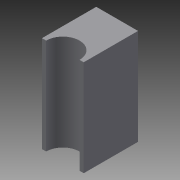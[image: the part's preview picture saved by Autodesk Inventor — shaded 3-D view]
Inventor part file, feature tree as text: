
AUTODESK INVENTOR PART (.ipt)
format: ipt  version: 2015 SP2 (Build 190223200, 223)  size: 78,336 bytes
history: native  units: mm
features: sketch x2, extrude x1, hole x1
ambient origin geometry x8: Origin, YZ Plane, XZ Plane, XY Plane, X Axis, Y Axis, Z Axis, Center Point
bodies: Solid1 (feature_tree)
feature tree (4):
  extrude  "Extrusion1"  Depth=23.0mm
  hole  "Hole1"  [1 undecoded]
  sketch  "Sketch1"  dims[d0=10.0mm d1=23.0mm]
  sketch  "Sketch4"  dims[d2=13.0mm d3=0.0mm d11=8.0mm d12=8.0mm d13=6.0mm d14=4.0mm d15=2.0mm d16=90.0deg d17=8.0mm d18=20.594885mm]
note: 1 required parameter value undecoded (feature->parameter linkage not recoverable at this tier; creation-order binding heuristic only, values carry confidence <= 0.55)
